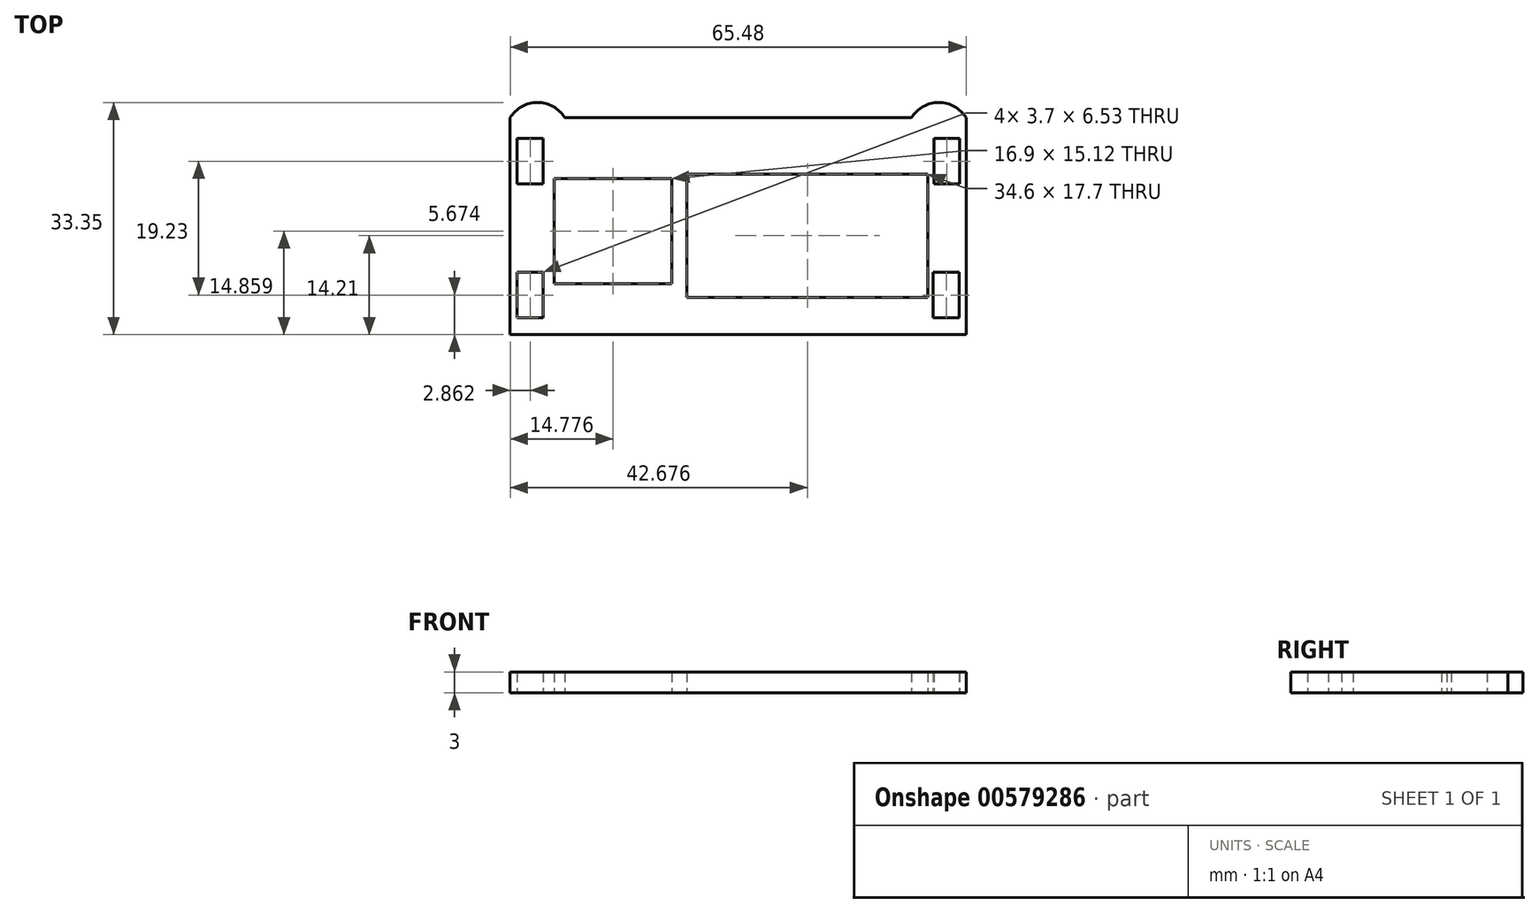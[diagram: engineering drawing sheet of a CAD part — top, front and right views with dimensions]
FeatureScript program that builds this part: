
annotation { "Feature Type Name" : "Feature", "Feature Type Description" : "" }
export const myFeature = defineFeature(function(context is Context, id is Id, definition is map)
    precondition{}
    {
        {
            var Q0;
            Q0=qCreatedBy(makeId("Top.planeOp"),FACE);
            var sketch = newSketch(context, id + "F0", { "sketchPlane" : qUnion([Q0])});
            skLineSegment(sketch, "E0.top", {"start": v(-28.68, -21.55) * mm, "end": v(36.89, -21.55) * mm});
            skLineSegment(sketch, "E0.left", {"start": v(-28.68, 9.62) * mm, "end": v(-28.68, -21.55) * mm});
            skLineSegment(sketch, "E0.right", {"start": v(36.89, 9.62) * mm, "end": v(36.89, -21.55) * mm});
            skArc(sketch, "E1", {"start": v(-20.83, 9.62) * mm, "mid": v(-24.76, 11.8) * mm, "end": v(-28.68, 9.62) * mm});
            skPoint(sketch, "E2.end.orphan", {"position": v(-24.76, 11.8) * mm});
            skPoint(sketch, "E3.start.orphan", {"position": v(-24.76, 9.62) * mm});
            skLineSegment(sketch, "E4.bottom", {"start": v(-27.67, -12.61) * mm, "end": v(-23.97, -12.61) * mm});
            skLineSegment(sketch, "E4.top", {"start": v(-27.67, -19.14) * mm, "end": v(-23.97, -19.14) * mm});
            skLineSegment(sketch, "E4.left", {"start": v(-27.67, -12.61) * mm, "end": v(-27.67, -19.14) * mm});
            skLineSegment(sketch, "E4.right", {"start": v(-23.97, -12.61) * mm, "end": v(-23.97, -19.14) * mm});
            skLineSegment(sketch, "E5.bottom", {"start": v(-27.67, 6.62) * mm, "end": v(-23.97, 6.62) * mm});
            skLineSegment(sketch, "E5.top", {"start": v(-27.67, 0.09) * mm, "end": v(-23.97, 0.09) * mm});
            skLineSegment(sketch, "E5.left", {"start": v(-27.67, 6.62) * mm, "end": v(-27.67, 0.09) * mm});
            skLineSegment(sketch, "E5.right", {"start": v(-23.97, 6.62) * mm, "end": v(-23.97, 0.09) * mm});
            skPoint(sketch, "E6.MirrorP", {"position": v(32.87, 9.62) * mm});
            skArc(sketch, "E7.MirrorCS", {"start": v(28.95, 9.62) * mm, "mid": v(32.87, 11.8) * mm, "end": v(36.8, 9.62) * mm});
            skPoint(sketch, "E8.MirrorP", {"position": v(32.87, 11.8) * mm});
            skLineSegment(sketch, "E9.MirrorCS", {"start": v(36.8, 9.62) * mm, "end": v(36.8, -21.55) * mm});
            skLineSegment(sketch, "E10", {"start": v(-20.83, 9.62) * mm, "end": v(28.95, 9.62) * mm});
            skLineSegment(sketch, "E11.bottom", {"start": v(-22.35, 0.87) * mm, "end": v(-5.45, 0.87) * mm});
            skLineSegment(sketch, "E11.top", {"start": v(-22.35, -14.25) * mm, "end": v(-5.45, -14.25) * mm});
            skLineSegment(sketch, "E11.left", {"start": v(-22.35, 0.87) * mm, "end": v(-22.35, -14.25) * mm});
            skLineSegment(sketch, "E11.right", {"start": v(-5.45, 0.87) * mm, "end": v(-5.45, -14.25) * mm});
            skLineSegment(sketch, "E12.bottom", {"start": v(-3.3, 1.51) * mm, "end": v(31.3, 1.51) * mm});
            skLineSegment(sketch, "E12.top", {"start": v(-3.3, -16.2) * mm, "end": v(31.3, -16.2) * mm});
            skLineSegment(sketch, "E12.left", {"start": v(-3.3, 1.51) * mm, "end": v(-3.3, -16.2) * mm});
            skLineSegment(sketch, "E12.right", {"start": v(31.3, 1.51) * mm, "end": v(31.3, -16.2) * mm});
            skLineSegment(sketch, "E13.MirrorCS", {"start": v(32.08, -12.61) * mm, "end": v(32.08, -19.14) * mm});
            skLineSegment(sketch, "E14.MirrorCS", {"start": v(35.87, 6.62) * mm, "end": v(32.17, 6.62) * mm});
            skLineSegment(sketch, "E15.MirrorCS", {"start": v(35.78, -19.14) * mm, "end": v(32.08, -19.14) * mm});
            skLineSegment(sketch, "E16.MirrorCS", {"start": v(35.78, -12.61) * mm, "end": v(35.78, -19.14) * mm});
            skLineSegment(sketch, "E17.MirrorCS", {"start": v(35.87, 0.09) * mm, "end": v(32.17, 0.09) * mm});
            skLineSegment(sketch, "E18.MirrorCS", {"start": v(35.78, -12.61) * mm, "end": v(32.08, -12.61) * mm});
            skLineSegment(sketch, "E19.MirrorCS", {"start": v(35.87, 6.62) * mm, "end": v(35.87, 0.09) * mm});
            skLineSegment(sketch, "E20.MirrorCS", {"start": v(32.17, 6.62) * mm, "end": v(32.17, 0.09) * mm});
            skSolve(sketch);
        }
        {
            var Q0;
            {var subQ1=sQuery(id+"F0.wireOp",EDGE,"E0.left");Q0=makeQuery(id+"F0.imprint","IMPRINT",FACE,{"disambiguationData":[TD([[makeQuery(id+"F0.imprint","IMPRINT",EDGE,{"derivedFrom":subQ1}),1.0]])]});}
            extrude(context, id + "F1", {"entities" : qUnion([Q0]), "depth" : 3 * mm, "offsetDistance" : 25.4 * mm});
        }
    });
